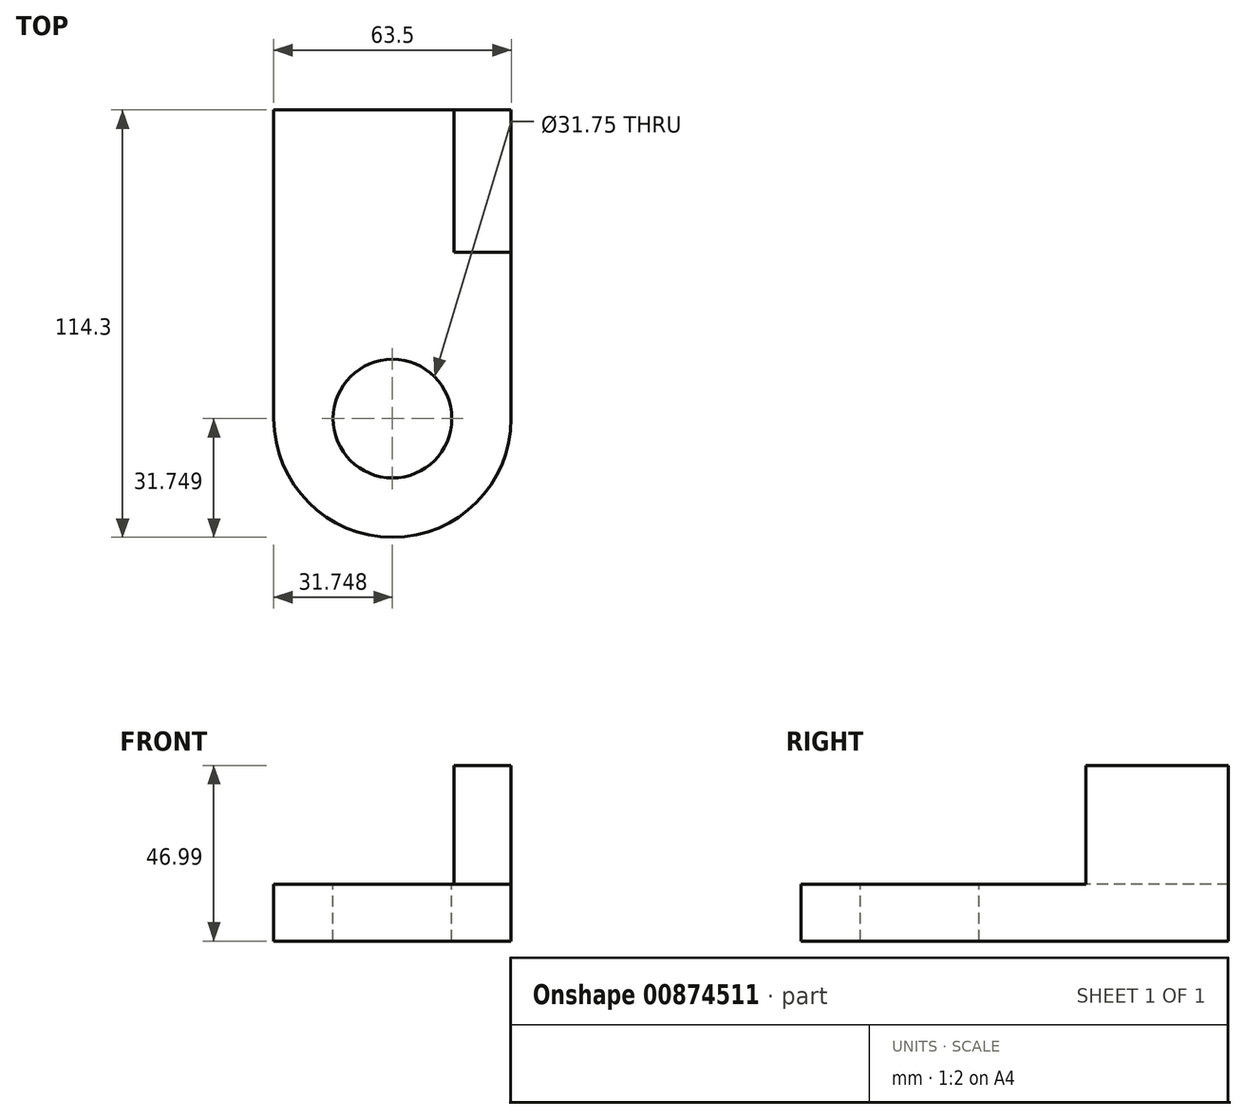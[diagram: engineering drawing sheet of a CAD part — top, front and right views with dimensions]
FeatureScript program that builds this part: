
annotation { "Feature Type Name" : "Feature", "Feature Type Description" : "" }
export const myFeature = defineFeature(function(context is Context, id is Id, definition is map)
    precondition{}
    {
        {
            var Q0;
            Q0=qCreatedBy(makeId("Top.planeOp"),FACE);
            var sketch = newSketch(context, id + "F0", { "sketchPlane" : qUnion([Q0])});
            skLineSegment(sketch, "E0.bottom", {"start": v(-22.45, 47.76) * mm, "end": v(41.05, 47.76) * mm});
            skLineSegment(sketch, "E0.top", {"start": v(-22.45, -34.8) * mm, "end": v(41.05, -34.8) * mm});
            skLineSegment(sketch, "E0.left", {"start": v(-22.45, 47.76) * mm, "end": v(-22.45, -34.8) * mm});
            skLineSegment(sketch, "E0.right", {"start": v(41.05, 47.76) * mm, "end": v(41.05, -34.8) * mm});
            skSolve(sketch);
        }
        {
            var Q0;
            Q0=makeQuery(id+"F0.imprint","IMPRINT",FACE,{"disambiguationData":[TD([[makeQuery(id+"F0.imprint","IMPRINT",EDGE,{"derivedFrom":sQuery(id+"F0.wireOp",EDGE,"E0.bottom")}),-1.0]])]});
            extrude(context, id + "F1", {"entities" : qUnion([Q0]), "depth" : 15.24 * mm, "offsetDistance" : 25.4 * mm});
        }
        {
            var Q0;
            Q0=makeQuery(id+"F1.opExtrude","CAP_FACE",FACE,{"disambiguationData":[OSD([sQuery(id+"F0.wireOp",EDGE,"E0.bottom"),sQuery(id+"F0.wireOp",EDGE,"E0.top"),sQuery(id+"F0.wireOp",EDGE,"E0.left"),sQuery(id+"F0.wireOp",EDGE,"E0.right")])],"isStart":false});
            var sketch = newSketch(context, id + "F2", { "sketchPlane" : qUnion([Q0])});
            skLineSegment(sketch, "E1", {"start": v(41.05, 47.76) * mm, "end": v(25.8, 47.76) * mm});
            skLineSegment(sketch, "E2", {"start": v(25.8, 47.76) * mm, "end": v(25.8, 9.66) * mm});
            skLineSegment(sketch, "E3", {"start": v(25.8, 9.66) * mm, "end": v(41.05, 9.66) * mm});
            skLineSegment(sketch, "E4", {"start": v(41.05, 9.66) * mm, "end": v(41.05, 47.76) * mm});
            skSolve(sketch);
        }
        {
            var Q0;
            Q0=makeQuery(id+"F2.imprint","IMPRINT",FACE,{"disambiguationData":[TD([[makeQuery(id+"F2.imprint","IMPRINT",EDGE,{"derivedFrom":sQuery(id+"F2.wireOp",EDGE,"E1")}),-1.0]])]});
            extrude(context, id + "F3", {"entities" : qUnion([Q0]), "operationType" : NewBodyOperationType.ADD, "depth" : 31.75 * mm, "offsetDistance" : 25.4 * mm});
        }
        {
            var Q0;
            Q0=makeQuery(id+"F1.opExtrude","CAP_FACE",FACE,{"disambiguationData":[OSD([sQuery(id+"F0.wireOp",EDGE,"E0.bottom"),sQuery(id+"F0.wireOp",EDGE,"E0.top"),sQuery(id+"F0.wireOp",EDGE,"E0.left"),sQuery(id+"F0.wireOp",EDGE,"E0.right")])],"isStart":false});
            var sketch = newSketch(context, id + "F4", { "sketchPlane" : qUnion([Q0])});
            skLineSegment(sketch, "E5", {"start": v(-22.45, -34.8) * mm, "end": v(9.3, -34.8) * mm});
            skCircle(sketch, "E6", {"center": v(9.3, -34.8) * mm, "radius": 15.88 * mm});
            skLineSegment(sketch, "E7", {"start": v(-22.45, -34.8) * mm, "end": v(-22.45, -66.54) * mm});
            skLineSegment(sketch, "E8", {"start": v(-22.45, -66.54) * mm, "end": v(41.05, -66.54) * mm});
            skLineSegment(sketch, "E9", {"start": v(41.05, -66.54) * mm, "end": v(41.05, -34.8) * mm});
            skSolve(sketch);
        }
        {
            var Q0;
            {var subQ0=sQuery(id+"F4.wireOp",EDGE,"E7");Q0=makeQuery(id+"F4.imprint","IMPRINT",FACE,{"disambiguationData":[TD([[makeQuery(id+"F4.imprint","IMPRINT",EDGE,{"derivedFrom":subQ0}),1.0]])]});}
            extrude(context, id + "F5", {"entities" : qUnion([Q0]), "operationType" : NewBodyOperationType.ADD, "oppositeDirection" : true, "depth" : 15.24 * mm, "offsetDistance" : 25.4 * mm});
        }
        {
            var Q0;
            {var subQ0=sQuery(id+"F0.wireOp",EDGE,"E0.top");Q0=makeQuery(id+"F5.boolean.opBoolean","MERGE",FACE,{"derivedFrom":[makeQuery(id+"F1.opExtrude","CAP_FACE",FACE,{"disambiguationData":[OSD([sQuery(id+"F0.wireOp",EDGE,"E0.bottom"),subQ0,sQuery(id+"F0.wireOp",EDGE,"E0.left"),sQuery(id+"F0.wireOp",EDGE,"E0.right")])],"isStart":false}),makeQuery(id+"F5.opExtrude","CAP_FACE",FACE,{"disambiguationData":[OSD([subQ0,sQuery(id+"F4.wireOp",EDGE,"E5"),sQuery(id+"F4.wireOp",EDGE,"E6"),sQuery(id+"F4.wireOp",EDGE,"E7"),sQuery(id+"F4.wireOp",EDGE,"E8"),sQuery(id+"F4.wireOp",EDGE,"E9")])],"isStart":true})]});}
            var sketch = newSketch(context, id + "F6", { "sketchPlane" : qUnion([Q0])});
            skCircle(sketch, "E10", {"center": v(9.3, -34.8) * mm, "radius": 15.88 * mm});
            skSolve(sketch);
        }
        {
            var Q0;
            {var subQ1=makeQuery(id+"F1.opExtrude","CAP_EDGE",EDGE,{"disambiguationData":[OSD([sQuery(id+"F0.wireOp",EDGE,"E0.top")])],"isStart":false});Q0=makeQuery(id+"F6.imprint","IMPRINT",FACE,{"disambiguationData":[TD([[makeQuery(id+"F6.imprint","IMPRINT",EDGE,{"derivedFrom":subQ1}),1.0]])]});}
            extrude(context, id + "F7", {"entities" : qUnion([Q0]), "operationType" : NewBodyOperationType.REMOVE, "oppositeDirection" : true, "depth" : 25.4 * mm, "offsetDistance" : 25.4 * mm});
        }
        {
            var Q0;
            Q0=makeQuery(id+"F5.opExtrude","SWEPT_EDGE",EDGE,{"disambiguationData":[OSD([sQuery(id+"F4.wireOp",EDGE,"E8"),sQuery(id+"F4.wireOp",EDGE,"E9")])]});
            var Q1;
            Q1=makeQuery(id+"F5.opExtrude","SWEPT_EDGE",EDGE,{"disambiguationData":[OSD([sQuery(id+"F4.wireOp",EDGE,"E7"),sQuery(id+"F4.wireOp",EDGE,"E8")])]});
            fillet(context, id + "F8", {"entities" : qUnion([Q0, Q1]), "radius" : 31.75 * mm, "tangentPropagation" : true, "allowEdgeOverflow" : false});
        }
    });
